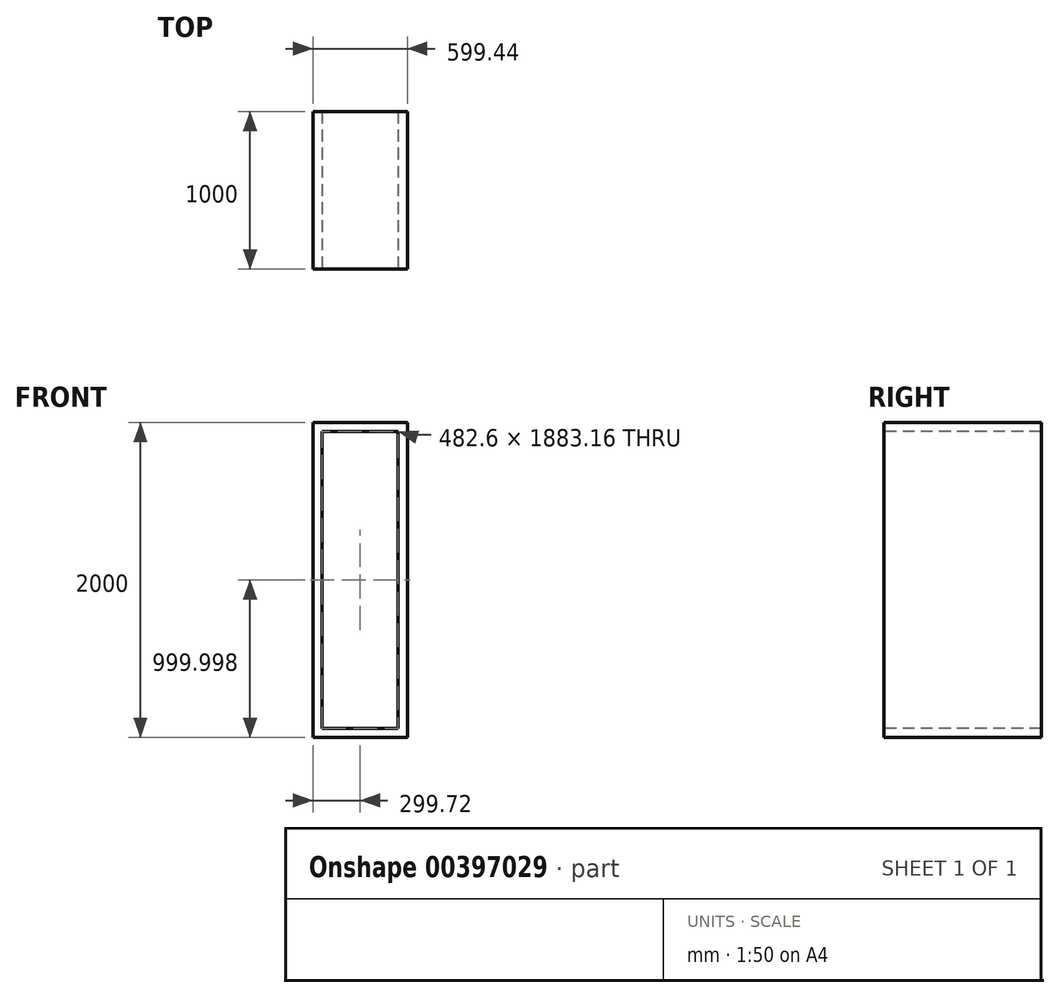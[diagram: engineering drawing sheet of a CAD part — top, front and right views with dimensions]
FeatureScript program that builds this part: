
annotation { "Feature Type Name" : "Feature", "Feature Type Description" : "" }
export const myFeature = defineFeature(function(context is Context, id is Id, definition is map)
    precondition{}
    {
        {
            var Q0;
            Q0=qCreatedBy(makeId("Top.planeOp"),FACE);
            var sketch = newSketch(context, id + "F0", { "sketchPlane" : qUnion([Q0])});
            skLineSegment(sketch, "E0.bottom", {"start": v(299.72, 500) * mm, "end": v(-299.72, 500) * mm});
            skLineSegment(sketch, "E0.top", {"start": v(299.72, -500) * mm, "end": v(-299.72, -500) * mm});
            skLineSegment(sketch, "E0.left", {"start": v(299.72, 500) * mm, "end": v(299.72, -500) * mm});
            skLineSegment(sketch, "E0.right", {"start": v(-299.72, 500) * mm, "end": v(-299.72, -500) * mm});
            skPoint(sketch, "E0.middle", {"position": v(0, 0) * mm});
            skSolve(sketch);
        }
        {
            var Q0;
            Q0 = qSketchRegion(id + "F0", true);
            extrude(context, id + "F1", {"entities" : qUnion([Q0]), "depth" : 2000 * mm, "offsetDistance" : 25.4 * mm});
        }
        {
            var Q0;
            Q0=makeQuery(id+"F1.opExtrude","SWEPT_FACE",FACE,{"disambiguationData":[OSD([sQuery(id+"F0.wireOp",EDGE,"E0.top")])]});
            var sketch = newSketch(context, id + "F2", { "sketchPlane" : qUnion([Q0])});
            skLineSegment(sketch, "E1.bottom", {"start": v(-241.3, 58.42) * mm, "end": v(241.3, 58.42) * mm});
            skLineSegment(sketch, "E1.top", {"start": v(-241.3, 1941.58) * mm, "end": v(241.3, 1941.58) * mm});
            skLineSegment(sketch, "E1.left", {"start": v(-241.3, 58.42) * mm, "end": v(-241.3, 1941.58) * mm});
            skLineSegment(sketch, "E1.right", {"start": v(241.3, 58.42) * mm, "end": v(241.3, 1941.58) * mm});
            skSolve(sketch);
        }
        {
            var Q0;
            Q0 = qSketchRegion(id + "F2", true);
            extrude(context, id + "F3", {"entities" : qUnion([Q0]), "operationType" : NewBodyOperationType.REMOVE, "endBound" : BoundingType.THROUGH_ALL, "oppositeDirection" : true, "depth" : 941.58 * mm, "offsetDistance" : 25.4 * mm});
        }
    });
